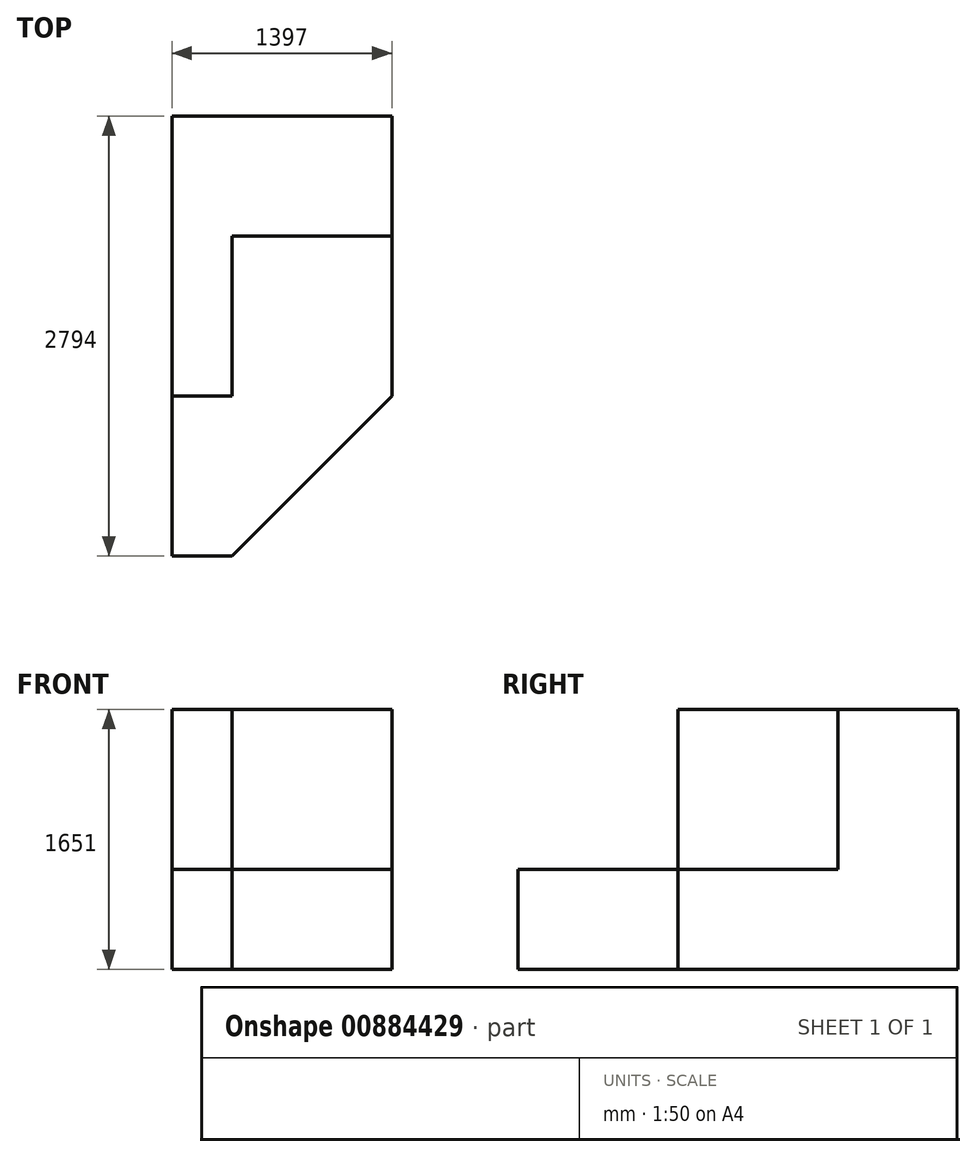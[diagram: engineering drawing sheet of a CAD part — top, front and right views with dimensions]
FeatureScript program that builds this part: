
annotation { "Feature Type Name" : "Feature", "Feature Type Description" : "" }
export const myFeature = defineFeature(function(context is Context, id is Id, definition is map)
    precondition{}
    {
        {
            var Q0;
            Q0=qCreatedBy(makeId("Top.planeOp"),FACE);
            var sketch = newSketch(context, id + "F0", { "sketchPlane" : qUnion([Q0])});
            skLineSegment(sketch, "E0.bottom", {"start": v(-962.15, 2746.2) * mm, "end": v(434.85, 2746.2) * mm});
            skLineSegment(sketch, "E0.top", {"start": v(-962.15, -47.8) * mm, "end": v(434.85, -47.8) * mm});
            skLineSegment(sketch, "E0.left", {"start": v(-962.15, 2746.2) * mm, "end": v(-962.15, -47.8) * mm});
            skLineSegment(sketch, "E0.right", {"start": v(434.85, 2746.2) * mm, "end": v(434.85, -47.8) * mm});
            skLineSegment(sketch, "E1", {"start": v(434.85, -47.8) * mm, "end": v(-581.15, -47.8) * mm});
            skLineSegment(sketch, "E2", {"start": v(434.85, -47.8) * mm, "end": v(434.85, 968.2) * mm});
            skLineSegment(sketch, "E3", {"start": v(434.85, 968.2) * mm, "end": v(-581.15, -47.8) * mm});
            skSolve(sketch);
        }
        {
            var Q0;
            Q0=makeQuery(id+"F0.imprint","IMPRINT",FACE,{"disambiguationData":[TD([[makeQuery(id+"F0.imprint","IMPRINT",EDGE,{"derivedFrom":sQuery(id+"F0.wireOp",EDGE,"E0.bottom")}),-1.0]])]});
            extrude(context, id + "F1", {"entities" : qUnion([Q0]), "depth" : 635 * mm, "offsetDistance" : 25.4 * mm});
        }
        {
            var Q0;
            Q0=makeQuery(id+"F1.opExtrude","CAP_FACE",FACE,{"disambiguationData":[OSD([sQuery(id+"F0.wireOp",EDGE,"E0.bottom"),sQuery(id+"F0.wireOp",EDGE,"E0.top"),sQuery(id+"F0.wireOp",EDGE,"E0.left"),sQuery(id+"F0.wireOp",EDGE,"E0.right"),sQuery(id+"F0.wireOp",EDGE,"E3")])],"isStart":false});
            var sketch = newSketch(context, id + "F2", { "sketchPlane" : qUnion([Q0])});
            skLineSegment(sketch, "E4.bottom", {"start": v(-962.15, 2746.2) * mm, "end": v(434.85, 2746.2) * mm});
            skLineSegment(sketch, "E4.top", {"start": v(-962.15, 968.2) * mm, "end": v(434.85, 968.2) * mm});
            skLineSegment(sketch, "E4.left", {"start": v(-962.15, 2746.2) * mm, "end": v(-962.15, 968.2) * mm});
            skLineSegment(sketch, "E4.right", {"start": v(434.85, 2746.2) * mm, "end": v(434.85, 968.2) * mm});
            skSolve(sketch);
        }
        {
            var Q0;
            Q0=makeQuery(id+"F2.imprint","IMPRINT",FACE,{"disambiguationData":[TD([[makeQuery(id+"F2.imprint","IMPRINT",EDGE,{"derivedFrom":sQuery(id+"F2.wireOp",EDGE,"E4.bottom")}),-1.0]])]});
            extrude(context, id + "F3", {"entities" : qUnion([Q0]), "operationType" : NewBodyOperationType.ADD, "depth" : 1016 * mm, "offsetDistance" : 25.4 * mm});
        }
        {
            var Q0;
            Q0=makeQuery(id+"F3.opExtrude","CAP_FACE",FACE,{"disambiguationData":[OSD([sQuery(id+"F2.wireOp",EDGE,"E4.bottom"),sQuery(id+"F2.wireOp",EDGE,"E4.top"),sQuery(id+"F2.wireOp",EDGE,"E4.left"),sQuery(id+"F2.wireOp",EDGE,"E4.right")])],"isStart":false});
            var sketch = newSketch(context, id + "F4", { "sketchPlane" : qUnion([Q0])});
            skLineSegment(sketch, "E5.bottom", {"start": v(434.85, 968.2) * mm, "end": v(-581.15, 968.2) * mm});
            skLineSegment(sketch, "E5.top", {"start": v(434.85, 1984.2) * mm, "end": v(-581.15, 1984.2) * mm});
            skLineSegment(sketch, "E5.left", {"start": v(434.85, 968.2) * mm, "end": v(434.85, 1984.2) * mm});
            skLineSegment(sketch, "E5.right", {"start": v(-581.15, 968.2) * mm, "end": v(-581.15, 1984.2) * mm});
            skSolve(sketch);
        }
        {
            var Q0;
            Q0=makeQuery(id+"F4.imprint","IMPRINT",FACE,{"disambiguationData":[TD([[makeQuery(id+"F4.imprint","IMPRINT",EDGE,{"derivedFrom":sQuery(id+"F4.wireOp",EDGE,"E5.bottom")}),1.0]])]});
            extrude(context, id + "F5", {"entities" : qUnion([Q0]), "operationType" : NewBodyOperationType.REMOVE, "oppositeDirection" : true, "depth" : 1016 * mm, "offsetDistance" : 25.4 * mm});
        }
    });
